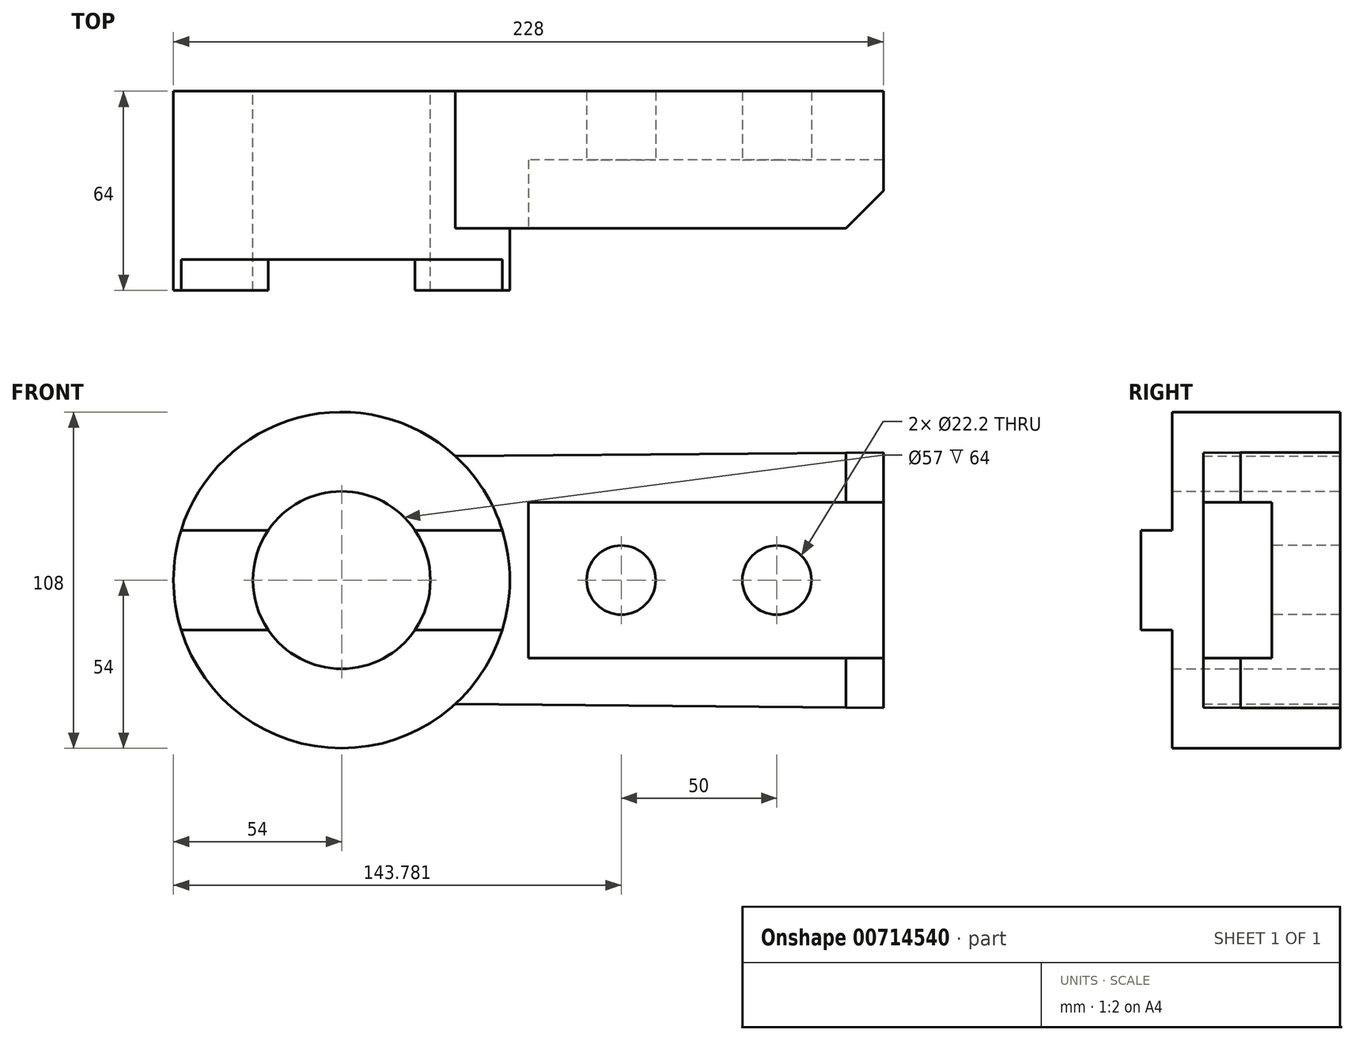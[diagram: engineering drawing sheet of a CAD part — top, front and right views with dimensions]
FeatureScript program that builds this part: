
annotation { "Feature Type Name" : "Feature", "Feature Type Description" : "" }
export const myFeature = defineFeature(function(context is Context, id is Id, definition is map)
    precondition{}
    {
        {
            var Q0;
            Q0=qCreatedBy(makeId("Front.planeOp"),FACE);
            var sketch = newSketch(context, id + "F0", { "sketchPlane" : qUnion([Q0])});
            skCircle(sketch, "E0", {"center": v(0, 0) * mm, "radius": 54 * mm});
            skCircle(sketch, "E1", {"center": v(0, 0) * mm, "radius": 28.5 * mm});
            skSolve(sketch);
        }
        {
            var Q0;
            Q0=makeQuery(id+"F0.imprint","IMPRINT",FACE,{"disambiguationData":[TD([[makeQuery(id+"F0.imprint","IMPRINT",EDGE,{"derivedFrom":sQuery(id+"F0.wireOp",EDGE,"E0")}),1.0]])]});
            extrude(context, id + "F1", {"entities" : qUnion([Q0]), "depth" : 54 * mm, "offsetDistance" : 25 * mm});
        }
        {
            var Q0;
            Q0=makeQuery(id+"F1.opExtrude","CAP_FACE",FACE,{"disambiguationData":[OSD([sQuery(id+"F0.wireOp",EDGE,"E0"),sQuery(id+"F0.wireOp",EDGE,"E1")])],"isStart":false});
            var sketch = newSketch(context, id + "F2", { "sketchPlane" : qUnion([Q0])});
            skCircle(sketch, "E2", {"center": v(0, 0) * mm, "radius": 54 * mm});
            skCircle(sketch, "E3", {"center": v(0, 0) * mm, "radius": 28.5 * mm});
            skLineSegment(sketch, "E4", {"start": v(-23.58, 16) * mm, "end": v(-51.58, 16) * mm});
            skLineSegment(sketch, "E5", {"start": v(-23.58, -16) * mm, "end": v(-51.58, -16) * mm});
            skLineSegment(sketch, "E6", {"start": v(23.58, 16) * mm, "end": v(51.58, 16) * mm});
            skLineSegment(sketch, "E7", {"start": v(23.58, -16) * mm, "end": v(51.58, -16) * mm});
            skSolve(sketch);
        }
        {
            var Q0;
            {var subQ0=sQuery(id+"F2.wireOp",EDGE,"E4");Q0=makeQuery(id+"F2.imprint","IMPRINT",FACE,{"disambiguationData":[TD([[makeQuery(id+"F2.imprint","IMPRINT",EDGE,{"derivedFrom":subQ0}),1.0]])]});}
            var Q1;
            {var subQ0=sQuery(id+"F2.wireOp",EDGE,"E6");Q1=makeQuery(id+"F2.imprint","IMPRINT",FACE,{"disambiguationData":[TD([[makeQuery(id+"F2.imprint","IMPRINT",EDGE,{"derivedFrom":subQ0}),-1.0]])]});}
            extrude(context, id + "F3", {"entities" : qUnion([Q0, Q1]), "operationType" : NewBodyOperationType.ADD, "depth" : 10 * mm, "offsetDistance" : 25 * mm});
        }
        {
            var Q0;
            Q0=makeQuery(id+"F1.opExtrude","CAP_FACE",FACE,{"disambiguationData":[OSD([sQuery(id+"F0.wireOp",EDGE,"E0"),sQuery(id+"F0.wireOp",EDGE,"E1")])],"isStart":true});
            var sketch = newSketch(context, id + "F4", { "sketchPlane" : qUnion([Q0])});
            skArc(sketch, "E8", {"start": v(-35.96, 39.78) * mm, "mid": v(-48.87, 21.72) * mm, "end": v(-53.44, 0) * mm});
            skLineSegment(sketch, "E9", {"start": v(-174, 0) * mm, "end": v(-174, 41) * mm});
            skLineSegment(sketch, "E10", {"start": v(-174, 41) * mm, "end": v(-35.96, 39.78) * mm});
            skLineSegment(sketch, "E11.MirrorCS", {"start": v(-174, -41) * mm, "end": v(-35.96, -39.78) * mm});
            skLineSegment(sketch, "E12.MirrorCS", {"start": v(-174, 0) * mm, "end": v(-174, -41) * mm});
            skSolve(sketch);
        }
        {
            var Q0;
            {var subQ5=sQuery(id+"F4.wireOp",EDGE,"E9");Q0=makeQuery(id+"F4.imprint","IMPRINT",FACE,{"disambiguationData":[TD([[makeQuery(id+"F4.imprint","IMPRINT",EDGE,{"derivedFrom":subQ5}),-1.0]])]});}
            extrude(context, id + "F5", {"entities" : qUnion([Q0]), "operationType" : NewBodyOperationType.ADD, "oppositeDirection" : true, "depth" : 44 * mm, "offsetDistance" : 25 * mm});
        }
        {
            var Q0;
            Q0=makeQuery(id+"F5.opExtrude","CAP_FACE",FACE,{"disambiguationData":[OSD([sQuery(id+"F0.wireOp",EDGE,"E0"),sQuery(id+"F4.wireOp",EDGE,"E9"),sQuery(id+"F4.wireOp",EDGE,"E10"),sQuery(id+"F4.wireOp",EDGE,"E11.MirrorCS"),sQuery(id+"F4.wireOp",EDGE,"E12.MirrorCS")])],"isStart":false});
            var sketch = newSketch(context, id + "F6", { "sketchPlane" : qUnion([Q0])});
            skLineSegment(sketch, "E13", {"start": v(174, -41) * mm, "end": v(174, -25) * mm});
            skLineSegment(sketch, "E14", {"start": v(174, -25) * mm, "end": v(60, -25) * mm});
            skLineSegment(sketch, "E15", {"start": v(60, -25) * mm, "end": v(60, 25) * mm});
            skLineSegment(sketch, "E16", {"start": v(60, 25) * mm, "end": v(174, 25) * mm});
            skSolve(sketch);
        }
        {
            var Q0;
            {var subQ0=sQuery(id+"F6.wireOp",EDGE,"E14");Q0=makeQuery(id+"F6.imprint","IMPRINT",FACE,{"disambiguationData":[TD([[makeQuery(id+"F6.imprint","IMPRINT",EDGE,{"derivedFrom":subQ0}),-1.0]])]});}
            extrude(context, id + "F7", {"entities" : qUnion([Q0]), "operationType" : NewBodyOperationType.REMOVE, "oppositeDirection" : true, "depth" : 22 * mm, "offsetDistance" : 25 * mm});
        }
        {
            var Q0;
            {var subQ0=sQuery(id+"F4.wireOp",EDGE,"E12.MirrorCS");var subQ1=sQuery(id+"F4.wireOp",EDGE,"E10");var subQ2=sQuery(id+"F4.wireOp",EDGE,"E9");Q0=makeQuery(id+"F7.boolean.opBoolean","SPLIT",EDGE,{"disambiguationData":[TD([makeQuery(id+"F5.opExtrude","SWEPT_FACE",FACE,{"disambiguationData":[OSD([subQ1])]})])],"derivedFrom":makeQuery(id+"F5.opExtrude","CAP_EDGE",EDGE,{"disambiguationData":[OSD([subQ2,subQ0])],"isStart":false})});}
            var Q1;
            {var subQ0=sQuery(id+"F4.wireOp",EDGE,"E12.MirrorCS");var subQ1=sQuery(id+"F4.wireOp",EDGE,"E11.MirrorCS");var subQ2=sQuery(id+"F4.wireOp",EDGE,"E9");Q1=makeQuery(id+"F7.boolean.opBoolean","SPLIT",EDGE,{"disambiguationData":[TD([makeQuery(id+"F5.opExtrude","SWEPT_FACE",FACE,{"disambiguationData":[OSD([subQ1])]})])],"derivedFrom":makeQuery(id+"F5.opExtrude","CAP_EDGE",EDGE,{"disambiguationData":[OSD([subQ2,subQ0])],"isStart":false})});}
            chamfer(context, id + "F8", {"entities" : qUnion([Q0, Q1]), "width" : 12 * mm, "tangentPropagation" : true});
        }
        {
            var Q0;
            Q0=makeQuery(id+"F7.boolean.opBoolean","COPY",FACE,{"derivedFrom":makeQuery(id+"F7.opExtrude","CAP_FACE",FACE,{"disambiguationData":[OSD([sQuery(id+"F4.wireOp",EDGE,"E9"),sQuery(id+"F4.wireOp",EDGE,"E12.MirrorCS"),sQuery(id+"F6.wireOp",EDGE,"E14"),sQuery(id+"F6.wireOp",EDGE,"E15"),sQuery(id+"F6.wireOp",EDGE,"E16")])],"isStart":false})});
            var sketch = newSketch(context, id + "F9", { "sketchPlane" : qUnion([Q0])});
            skCircle(sketch, "E17", {"center": v(139.78, 0) * mm, "radius": 11.1 * mm});
            skCircle(sketch, "E18", {"center": v(89.78, 0) * mm, "radius": 11.1 * mm});
            skSolve(sketch);
        }
        {
            var Q0;
            Q0 = qSketchRegion(id + "F9", true);
            extrude(context, id + "F10", {"entities" : qUnion([Q0]), "operationType" : NewBodyOperationType.REMOVE, "endBound" : BoundingType.UP_TO_NEXT, "oppositeDirection" : true, "depth" : 25 * mm, "offsetDistance" : 25 * mm});
        }
    });
